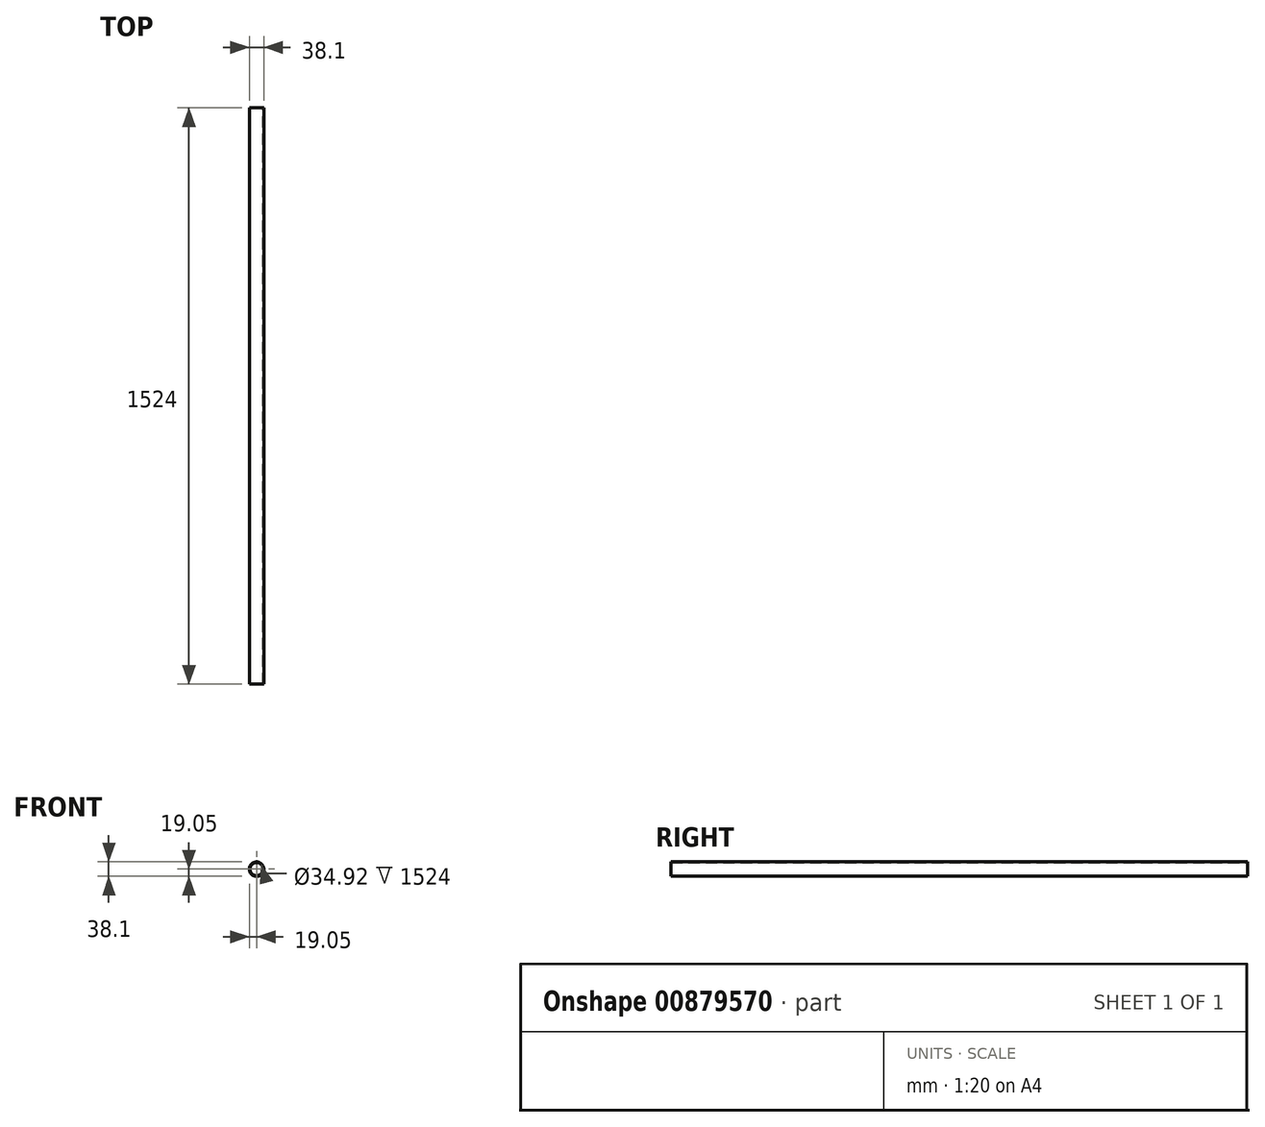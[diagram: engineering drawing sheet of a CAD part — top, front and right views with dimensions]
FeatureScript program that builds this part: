
annotation { "Feature Type Name" : "Feature", "Feature Type Description" : "" }
export const myFeature = defineFeature(function(context is Context, id is Id, definition is map)
    precondition{}
    {
        {
            var Q0;
            Q0=qCreatedBy(makeId("Front.planeOp"),FACE);
            var sketch = newSketch(context, id + "F0", { "sketchPlane" : qUnion([Q0])});
            skCircle(sketch, "E0", {"center": v(0, 0) * mm, "radius": 17.46 * mm});
            skCircle(sketch, "E1", {"center": v(0, 0) * mm, "radius": 19.05 * mm});
            skSolve(sketch);
        }
        {
            var Q0;
            Q0=makeQuery(id+"F0.imprint","IMPRINT",FACE,{"disambiguationData":[TD([[makeQuery(id+"F0.imprint","IMPRINT",EDGE,{"derivedFrom":sQuery(id+"F0.wireOp",EDGE,"E0")}),-1.0]])]});
            extrude(context, id + "F1", {"entities" : qUnion([Q0]), "endBound" : BoundingType.SYMMETRIC, "depth" : 1524 * mm, "offsetDistance" : 25.4 * mm});
        }
    });
